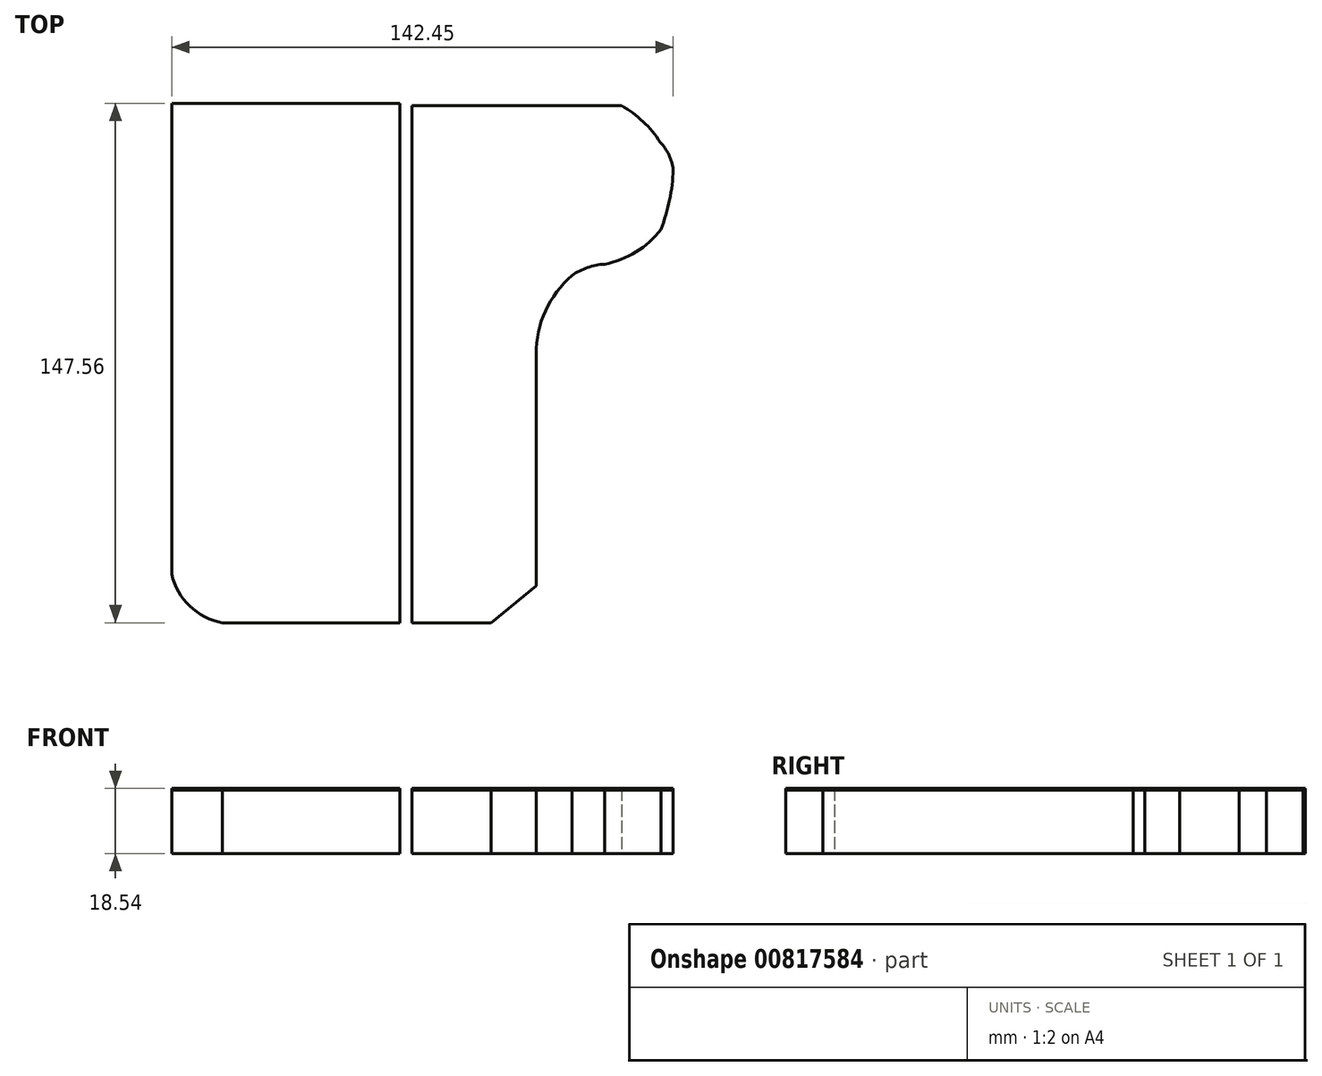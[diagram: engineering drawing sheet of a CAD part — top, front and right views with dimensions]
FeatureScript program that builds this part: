
annotation { "Feature Type Name" : "Feature", "Feature Type Description" : "" }
export const myFeature = defineFeature(function(context is Context, id is Id, definition is map)
    precondition{}
    {
        {
            var Q0;
            Q0=qCreatedBy(makeId("Top.planeOp"),FACE);
            var sketch = newSketch(context, id + "F0", { "sketchPlane" : qUnion([Q0])});
            skLineSegment(sketch, "E0.bottom", {"start": v(0, 73.7) * mm, "end": v(59.49, 73.7) * mm});
            skLineSegment(sketch, "E0.top", {"start": v(0, -73.22) * mm, "end": v(22.44, -73.22) * mm});
            skLineSegment(sketch, "E0.left", {"start": v(0, 73.7) * mm, "end": v(0, -73.22) * mm});
            skLineSegment(sketch, "E1", {"start": v(22.44, -73.22) * mm, "end": v(35.21, -62.68) * mm});
            skLineSegment(sketch, "E2", {"start": v(35.21, -62.68) * mm, "end": v(35.21, 3.11) * mm});
            skArc(sketch, "E3", {"start": v(45.43, 25.47) * mm, "mid": v(37.9, 15.4) * mm, "end": v(35.21, 3.11) * mm});
            skArc(sketch, "E4", {"start": v(54.7, 28.67) * mm, "mid": v(49.85, 27.7) * mm, "end": v(45.43, 25.47) * mm});
            skArc(sketch, "E5", {"start": v(54.7, 28.67) * mm, "mid": v(63.6, 32.13) * mm, "end": v(70.67, 38.57) * mm});
            skArc(sketch, "E6", {"start": v(70.67, 38.57) * mm, "mid": v(73.14, 46.88) * mm, "end": v(74.18, 55.5) * mm});
            skArc(sketch, "E7", {"start": v(74.18, 55.5) * mm, "mid": v(71.87, 61.57) * mm, "end": v(67.15, 66.04) * mm});
            skPoint(sketch, "E8.7.internal.orphan", {"position": v(23.08, 48.15) * mm});
            skPoint(sketch, "E8.9.internal.orphan", {"position": v(17, 46.55) * mm});
            skLineSegment(sketch, "E9", {"start": v(17.97, 55.5) * mm, "end": v(22.58, 57.38) * mm});
            skLineSegment(sketch, "E10", {"start": v(11.26, 59) * mm, "end": v(17.97, 55.5) * mm});
            skLineSegment(sketch, "E11.1.0", {"start": v(24.36, 59.55) * mm, "end": v(17.97, 55.5) * mm});
            skLineSegment(sketch, "E11.2.0", {"start": v(18.28, 47.93) * mm, "end": v(17.97, 55.5) * mm});
            skPoint(sketch, "E11.center", {"position": v(17.97, 55.5) * mm});
            skLineSegment(sketch, "E11.anchor1", {"start": v(17.97, 55.5) * mm, "end": v(11.26, 59) * mm, "construction": true});
            skLineSegment(sketch, "E11.anchor2", {"start": v(17.97, 55.5) * mm, "end": v(18.28, 47.93) * mm, "construction": true});
            skPoint(sketch, "E12.0.internal.orphan", {"position": v(39.69, 48.15) * mm});
            skPoint(sketch, "E12.1.internal.orphan", {"position": v(39.05, 54.27) * mm});
            skPoint(sketch, "E12.10.internal.orphan", {"position": v(63.64, 48.15) * mm});
            skPoint(sketch, "E12.13.internal.orphan", {"position": v(49.88, 38.89) * mm});
            skPoint(sketch, "E12.16.internal.orphan", {"position": v(41.28, 46.55) * mm});
            skPoint(sketch, "E12.17.internal.orphan", {"position": v(40, 46.55) * mm});
            skPoint(sketch, "E12.2.internal.orphan", {"position": v(40.64, 57.38) * mm});
            skPoint(sketch, "E12.5.internal.orphan", {"position": v(49.88, 62.84) * mm});
            skPoint(sketch, "E12.8.internal.orphan", {"position": v(62.04, 57.38) * mm});
            skPoint(sketch, "E12.9.internal.orphan", {"position": v(63.96, 54.27) * mm});
            skArc(sketch, "E13", {"start": v(74.18, 55.5) * mm, "mid": v(68.56, 66) * mm, "end": v(59.49, 73.7) * mm});
            skLineSegment(sketch, "E14.bottom", {"start": v(-68.27, 74.34) * mm, "end": v(-3.43, 74.34) * mm});
            skLineSegment(sketch, "E14.top", {"start": v(-53.9, -73.22) * mm, "end": v(-3.43, -73.22) * mm});
            skLineSegment(sketch, "E14.left", {"start": v(-68.27, 74.34) * mm, "end": v(-68.27, -59.37) * mm});
            skLineSegment(sketch, "E14.right", {"start": v(-3.43, 74.34) * mm, "end": v(-3.43, -73.22) * mm});
            skArc(sketch, "E15", {"start": v(-68.27, -59.37) * mm, "mid": v(-63.14, -68.43) * mm, "end": v(-53.9, -73.22) * mm});
            skSolve(sketch);
        }
        {
            var Q0;
            Q0 = qSketchRegion(id + "F0", true);
            extrude(context, id + "F1", {"entities" : qUnion([Q0]), "depth" : 18.54 * mm, "offsetDistance" : 25.4 * mm});
        }
        {
            var Q0;
            Q0 = qSketchRegion(id + "F0", true);
            extrude(context, id + "F2", {"entities" : qUnion([Q0]), "depth" : 18.03 * mm, "offsetDistance" : 25.4 * mm});
        }
    });
